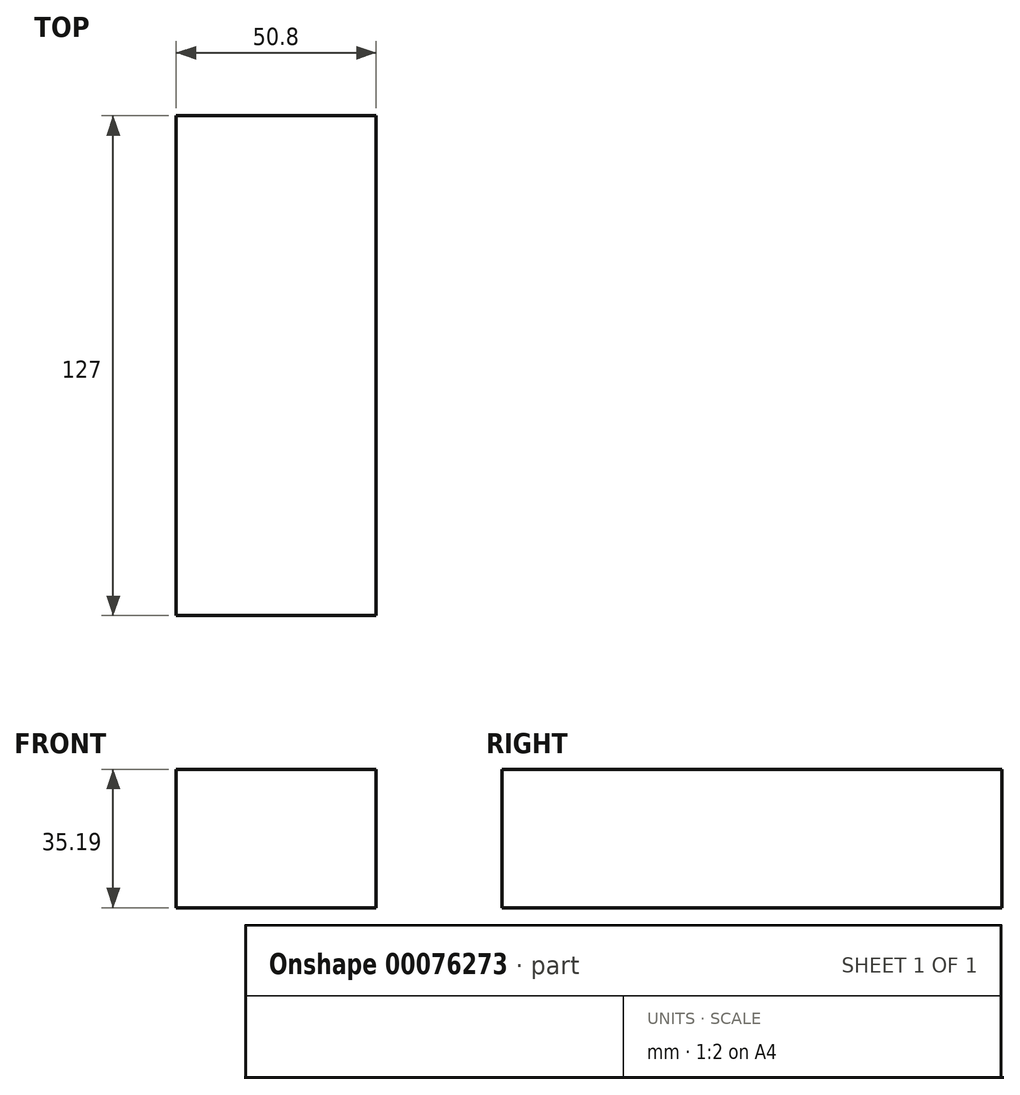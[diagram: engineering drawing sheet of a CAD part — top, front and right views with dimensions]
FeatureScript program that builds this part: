
annotation { "Feature Type Name" : "Feature", "Feature Type Description" : "" }
export const myFeature = defineFeature(function(context is Context, id is Id, definition is map)
    precondition{}
    {
        {
            var Q0;
            Q0=qCreatedBy(makeId("Front.planeOp"),FACE);
            var sketch = newSketch(context, id + "F0", { "sketchPlane" : qUnion([Q0])});
            skLineSegment(sketch, "E0.bottom", {"start": v(-25.4, 18.47) * mm, "end": v(25.4, 18.47) * mm});
            skLineSegment(sketch, "E0.top", {"start": v(-25.4, -16.72) * mm, "end": v(25.4, -16.72) * mm});
            skLineSegment(sketch, "E0.left", {"start": v(-25.4, 18.47) * mm, "end": v(-25.4, -16.72) * mm});
            skLineSegment(sketch, "E0.right", {"start": v(25.4, 18.47) * mm, "end": v(25.4, -16.72) * mm});
            skSolve(sketch);
        }
        {
            var Q0;
            Q0 = qSketchRegion(id + "F0", true);
            extrude(context, id + "F1", {"entities" : qUnion([Q0]), "depth" : 127 * mm});
        }
    });
